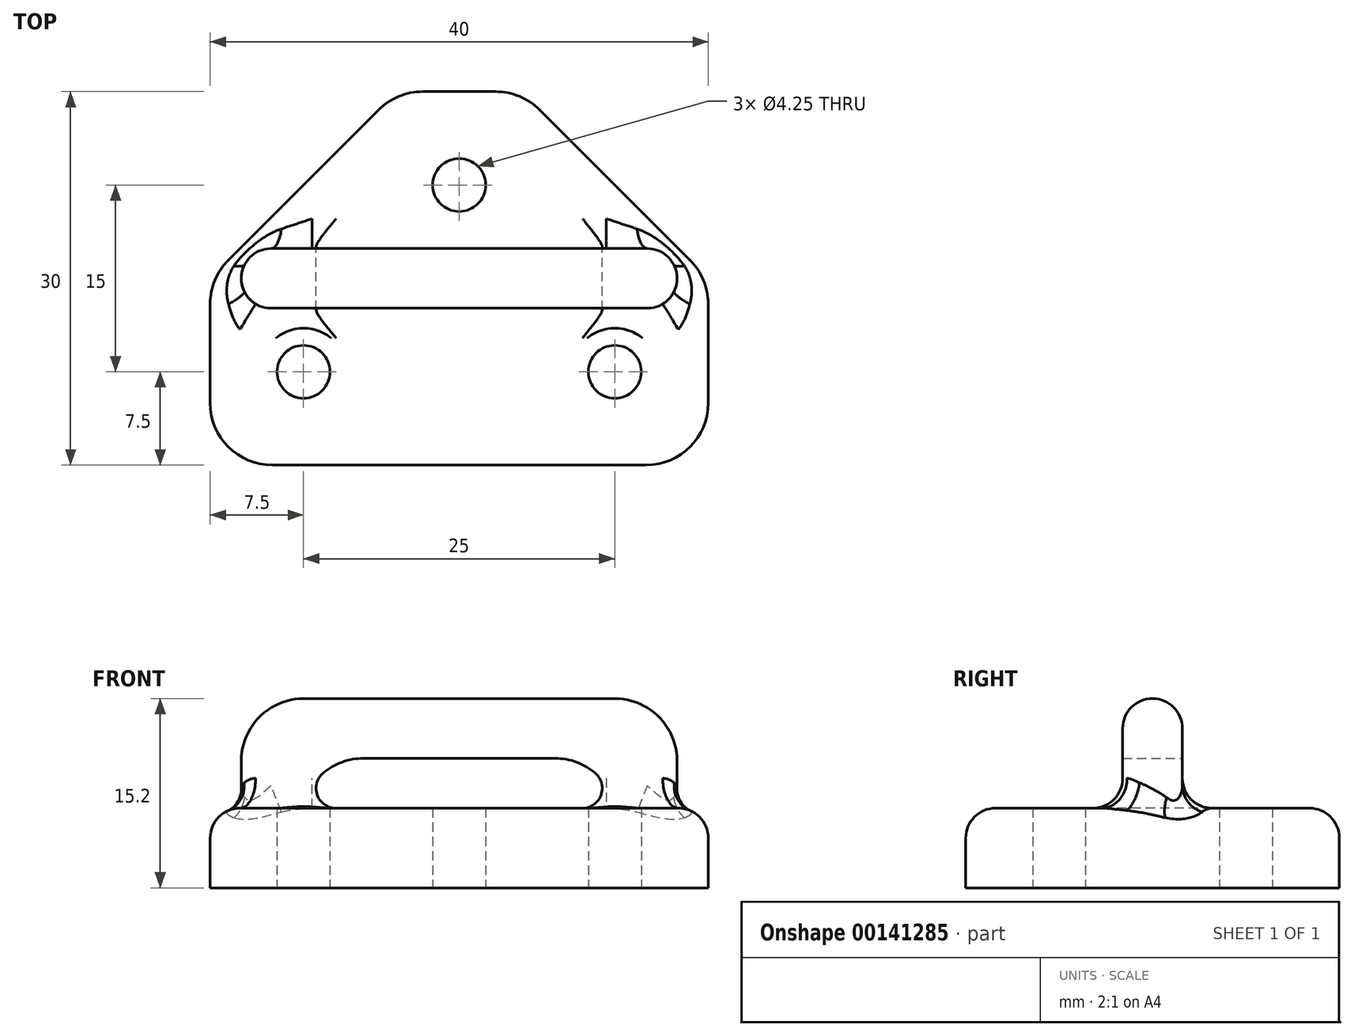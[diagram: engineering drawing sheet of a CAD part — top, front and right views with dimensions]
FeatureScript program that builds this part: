
annotation { "Feature Type Name" : "Feature", "Feature Type Description" : "" }
export const myFeature = defineFeature(function(context is Context, id is Id, definition is map)
    precondition{}
    {
        {
            var Q0;
            Q0=qCreatedBy(makeId("Top.planeOp"),FACE);
            var sketch = newSketch(context, id + "F0", { "sketchPlane" : qUnion([Q0])});
            skLineSegment(sketch, "E0.bottom", {"start": v(20, -15) * mm, "end": v(-20, -15) * mm});
            skLineSegment(sketch, "E0.top", {"start": v(20, 15) * mm, "end": v(-20, 15) * mm});
            skLineSegment(sketch, "E0.left", {"start": v(20, -15) * mm, "end": v(20, 15) * mm});
            skLineSegment(sketch, "E0.right", {"start": v(-20, -15) * mm, "end": v(-20, 15) * mm});
            skPoint(sketch, "E0.middle", {"position": v(0, 0) * mm});
            skCircle(sketch, "E1", {"center": v(0, 7.5) * mm, "radius": 2.12 * mm});
            skCircle(sketch, "E2", {"center": v(-12.5, -7.5) * mm, "radius": 2.12 * mm});
            skCircle(sketch, "E3.MirrorC", {"center": v(12.5, -7.5) * mm, "radius": 2.12 * mm});
            skSolve(sketch);
        }
        {
            var Q0;
            Q0 = qSketchRegion(id + "F0", true);
            extrude(context, id + "F1", {"entities" : qUnion([Q0]), "depth" : 6.4 * mm});
        }
        {
            var Q0;
            Q0=makeQuery(id+"F1.opExtrude","SWEPT_EDGE",EDGE,{"disambiguationData":[OSD([sQuery(id+"F0.wireOp",EDGE,"E0.top"),sQuery(id+"F0.wireOp",EDGE,"E0.right")])]});
            var Q1;
            Q1=makeQuery(id+"F1.opExtrude","SWEPT_EDGE",EDGE,{"disambiguationData":[OSD([sQuery(id+"F0.wireOp",EDGE,"E0.top"),sQuery(id+"F0.wireOp",EDGE,"E0.left")])]});
            chamfer(context, id + "F2", {"entities" : qUnion([Q0, Q1]), "width" : 15 * mm, "tangentPropagation" : true});
        }
        {
            var Q0;
            Q0=makeQuery(id+"F1.opExtrude","SWEPT_EDGE",EDGE,{"disambiguationData":[OSD([sQuery(id+"F0.wireOp",EDGE,"E0.bottom"),sQuery(id+"F0.wireOp",EDGE,"E0.right")])]});
            var Q1;
            Q1=makeQuery(id+"F1.opExtrude","SWEPT_EDGE",EDGE,{"disambiguationData":[OSD([sQuery(id+"F0.wireOp",EDGE,"E0.bottom"),sQuery(id+"F0.wireOp",EDGE,"E0.left")])]});
            var Q2;
            {var subQ0=sQuery(id+"F0.wireOp",EDGE,"E0.top");Q2=makeQuery(id+"F2.opChamfer","BLEND_EDGE",EDGE,{"blendedFrom":[makeQuery(id+"F1.opExtrude","SWEPT_EDGE",EDGE,{"disambiguationData":[OSD([subQ0,sQuery(id+"F0.wireOp",EDGE,"E0.right")])]}),makeQuery(id+"F1.opExtrude","SWEPT_FACE",FACE,{"disambiguationData":[OSD([subQ0])]})],"blendedInto":[makeQuery(id+"F1.opExtrude","SWEPT_FACE",FACE,{"disambiguationData":[OSD([subQ0])]})]});}
            var Q3;
            {var subQ0=sQuery(id+"F0.wireOp",EDGE,"E0.top");Q3=makeQuery(id+"F2.opChamfer","BLEND_EDGE",EDGE,{"blendedFrom":[makeQuery(id+"F1.opExtrude","SWEPT_EDGE",EDGE,{"disambiguationData":[OSD([subQ0,sQuery(id+"F0.wireOp",EDGE,"E0.left")])]}),makeQuery(id+"F1.opExtrude","SWEPT_FACE",FACE,{"disambiguationData":[OSD([subQ0])]})],"blendedInto":[makeQuery(id+"F1.opExtrude","SWEPT_FACE",FACE,{"disambiguationData":[OSD([subQ0])]})]});}
            var Q4;
            {var subQ0=sQuery(id+"F0.wireOp",EDGE,"E0.left");Q4=makeQuery(id+"F2.opChamfer","BLEND_EDGE",EDGE,{"blendedFrom":[makeQuery(id+"F1.opExtrude","SWEPT_EDGE",EDGE,{"disambiguationData":[OSD([sQuery(id+"F0.wireOp",EDGE,"E0.top"),subQ0])]}),makeQuery(id+"F1.opExtrude","SWEPT_FACE",FACE,{"disambiguationData":[OSD([subQ0])]})],"blendedInto":[makeQuery(id+"F1.opExtrude","SWEPT_FACE",FACE,{"disambiguationData":[OSD([subQ0])]})]});}
            var Q5;
            {var subQ0=sQuery(id+"F0.wireOp",EDGE,"E0.right");Q5=makeQuery(id+"F2.opChamfer","BLEND_EDGE",EDGE,{"blendedFrom":[makeQuery(id+"F1.opExtrude","SWEPT_EDGE",EDGE,{"disambiguationData":[OSD([sQuery(id+"F0.wireOp",EDGE,"E0.top"),subQ0])]}),makeQuery(id+"F1.opExtrude","SWEPT_FACE",FACE,{"disambiguationData":[OSD([subQ0])]})],"blendedInto":[makeQuery(id+"F1.opExtrude","SWEPT_FACE",FACE,{"disambiguationData":[OSD([subQ0])]})]});}
            fillet(context, id + "F3", {"entities" : qUnion([Q0, Q1, Q2, Q3, Q4, Q5]), "radius" : 5 * mm, "tangentPropagation" : true, "allowEdgeOverflow" : false});
        }
        {
            var Q0;
            Q0=qCreatedBy(makeId("Front.planeOp"),FACE);
            var sketch = newSketch(context, id + "F4", { "sketchPlane" : qUnion([Q0])});
            skLineSegment(sketch, "E4", {"start": v(-12.7, 6.4) * mm, "end": v(-17.5, 6.4) * mm});
            skLineSegment(sketch, "E5", {"start": v(-17.5, 6.4) * mm, "end": v(-17.5, 10.2) * mm});
            skLineSegment(sketch, "E6", {"start": v(-12.5, 15.2) * mm, "end": v(0, 15.2) * mm});
            skLineSegment(sketch, "E7", {"start": v(0, 10.4) * mm, "end": v(-7.7, 10.4) * mm});
            skLineSegment(sketch, "E8", {"start": v(-12.7, 6.4) * mm, "end": v(-12.7, 5.4) * mm});
            skPoint(sketch, "E9.orphan", {"position": v(0, 6.4) * mm});
            skLineSegment(sketch, "E10.MirrorCS", {"start": v(0, 10.4) * mm, "end": v(7.7, 10.4) * mm});
            skLineSegment(sketch, "E11.MirrorCS", {"start": v(17.5, 6.4) * mm, "end": v(17.5, 10.2) * mm});
            skLineSegment(sketch, "E12.MirrorCS", {"start": v(12.7, 6.4) * mm, "end": v(17.5, 6.4) * mm});
            skLineSegment(sketch, "E13.MirrorCS", {"start": v(12.5, 15.2) * mm, "end": v(0, 15.2) * mm});
            skLineSegment(sketch, "E14.MirrorCS", {"start": v(12.7, 6.4) * mm, "end": v(12.7, 5.4) * mm});
            skPoint(sketch, "E15.visualSharp", {"position": v(-17.5, 15.2) * mm});
            skArc(sketch, "E15.filletArc", {"start": v(-12.5, 15.2) * mm, "mid": v(-16.04, 13.74) * mm, "end": v(-17.5, 10.2) * mm});
            skPoint(sketch, "E16.visualSharp", {"position": v(17.5, 15.2) * mm});
            skArc(sketch, "E16.filletArc", {"start": v(17.5, 10.2) * mm, "mid": v(16.04, 13.74) * mm, "end": v(12.5, 15.2) * mm});
            skPoint(sketch, "E17.visualSharp", {"position": v(12.7, 10.4) * mm});
            skArc(sketch, "E17.filletArc", {"start": v(12.7, 5.4) * mm, "mid": v(11.24, 8.94) * mm, "end": v(7.7, 10.4) * mm});
            skPoint(sketch, "E18.visualSharp", {"position": v(-12.7, 10.4) * mm});
            skArc(sketch, "E18.filletArc", {"start": v(-7.7, 10.4) * mm, "mid": v(-11.24, 8.94) * mm, "end": v(-12.7, 5.4) * mm});
            skSolve(sketch);
        }
        {
            var Q0;
            Q0 = qSketchRegion(id + "F4", true);
            extrude(context, id + "F5", {"entities" : qUnion([Q0]), "operationType" : NewBodyOperationType.ADD, "endBound" : BoundingType.SYMMETRIC, "depth" : 4.8 * mm});
        }
        {
            var Q0;
            Q0=makeQuery(id+"F1.opExtrude","CAP_EDGE",EDGE,{"disambiguationData":[OSD([sQuery(id+"F0.wireOp",EDGE,"E0.top")])],"isStart":false});
            fillet(context, id + "F6", {"entities" : qUnion([Q0]), "radius" : 2.4 * mm, "tangentPropagation" : true, "allowEdgeOverflow" : false});
        }
        {
            var Q0;
            Q0=makeQuery(id+"F5.opExtrude","CAP_EDGE",EDGE,{"disambiguationData":[OSD([sQuery(id+"F4.wireOp",EDGE,"E6"),sQuery(id+"F4.wireOp",EDGE,"E13.MirrorCS")])],"isStart":true});
            var Q1;
            Q1=makeQuery(id+"F5.opExtrude","CAP_EDGE",EDGE,{"disambiguationData":[OSD([sQuery(id+"F4.wireOp",EDGE,"E6"),sQuery(id+"F4.wireOp",EDGE,"E13.MirrorCS")])],"isStart":false});
            fillet(context, id + "F7", {"entities" : qUnion([Q0, Q1]), "radius" : 2.4 * mm, "tangentPropagation" : true, "allowEdgeOverflow" : false});
        }
        {
            var Q0;
            Q0=makeQuery(id+"F5.boolean.opBoolean","INTERSECT",EDGE,{"derivedFrom":[makeQuery(id+"F1.opExtrude","CAP_FACE",FACE,{"disambiguationData":[OSD([sQuery(id+"F0.wireOp",EDGE,"E0.bottom"),sQuery(id+"F0.wireOp",EDGE,"E0.top"),sQuery(id+"F0.wireOp",EDGE,"E0.left"),sQuery(id+"F0.wireOp",EDGE,"E0.right"),sQuery(id+"F0.wireOp",EDGE,"E1"),sQuery(id+"F0.wireOp",EDGE,"E2"),sQuery(id+"F0.wireOp",EDGE,"E3.MirrorC")])],"isStart":false}),makeQuery(id+"F5.opExtrude","SWEPT_FACE",FACE,{"disambiguationData":[OSD([sQuery(id+"F4.wireOp",EDGE,"E17.filletArc")])]})]});
            var Q1;
            Q1=makeQuery(id+"F5.boolean.opBoolean","INTERSECT",EDGE,{"derivedFrom":[makeQuery(id+"F1.opExtrude","CAP_FACE",FACE,{"disambiguationData":[OSD([sQuery(id+"F0.wireOp",EDGE,"E0.bottom"),sQuery(id+"F0.wireOp",EDGE,"E0.top"),sQuery(id+"F0.wireOp",EDGE,"E0.left"),sQuery(id+"F0.wireOp",EDGE,"E0.right"),sQuery(id+"F0.wireOp",EDGE,"E1"),sQuery(id+"F0.wireOp",EDGE,"E2"),sQuery(id+"F0.wireOp",EDGE,"E3.MirrorC")])],"isStart":false}),makeQuery(id+"F5.opExtrude","SWEPT_FACE",FACE,{"disambiguationData":[OSD([sQuery(id+"F4.wireOp",EDGE,"E18.filletArc")])]})]});
            fillet(context, id + "F8", {"entities" : qUnion([Q0, Q1]), "radius" : 1.6 * mm, "tangentPropagation" : true, "allowEdgeOverflow" : false});
        }
        {
            var Q0;
            Q0=makeQuery(id+"F5.boolean.opBoolean","INTERSECT",EDGE,{"disambiguationData":[OD(0.0)],"derivedFrom":[makeQuery(id+"F1.opExtrude","CAP_FACE",FACE,{"disambiguationData":[OSD([sQuery(id+"F0.wireOp",EDGE,"E0.bottom"),sQuery(id+"F0.wireOp",EDGE,"E0.top"),sQuery(id+"F0.wireOp",EDGE,"E0.left"),sQuery(id+"F0.wireOp",EDGE,"E0.right"),sQuery(id+"F0.wireOp",EDGE,"E1"),sQuery(id+"F0.wireOp",EDGE,"E2"),sQuery(id+"F0.wireOp",EDGE,"E3.MirrorC")])],"isStart":false}),makeQuery(id+"F5.opExtrude","CAP_FACE",FACE,{"disambiguationData":[OSD([sQuery(id+"F4.wireOp",EDGE,"E4"),sQuery(id+"F4.wireOp",EDGE,"E5"),sQuery(id+"F4.wireOp",EDGE,"E6"),sQuery(id+"F4.wireOp",EDGE,"E7"),sQuery(id+"F4.wireOp",EDGE,"E8"),sQuery(id+"F4.wireOp",EDGE,"E10.MirrorCS"),sQuery(id+"F4.wireOp",EDGE,"E11.MirrorCS"),sQuery(id+"F4.wireOp",EDGE,"E12.MirrorCS"),sQuery(id+"F4.wireOp",EDGE,"E13.MirrorCS"),sQuery(id+"F4.wireOp",EDGE,"E14.MirrorCS"),sQuery(id+"F4.wireOp",EDGE,"E15.filletArc"),sQuery(id+"F4.wireOp",EDGE,"E16.filletArc"),sQuery(id+"F4.wireOp",EDGE,"E17.filletArc"),sQuery(id+"F4.wireOp",EDGE,"E18.filletArc")])],"isStart":false})]});
            var Q1;
            Q1=makeQuery(id+"F5.boolean.opBoolean","INTERSECT",EDGE,{"disambiguationData":[OD(1.0)],"derivedFrom":[makeQuery(id+"F1.opExtrude","CAP_FACE",FACE,{"disambiguationData":[OSD([sQuery(id+"F0.wireOp",EDGE,"E0.bottom"),sQuery(id+"F0.wireOp",EDGE,"E0.top"),sQuery(id+"F0.wireOp",EDGE,"E0.left"),sQuery(id+"F0.wireOp",EDGE,"E0.right"),sQuery(id+"F0.wireOp",EDGE,"E1"),sQuery(id+"F0.wireOp",EDGE,"E2"),sQuery(id+"F0.wireOp",EDGE,"E3.MirrorC")])],"isStart":false}),makeQuery(id+"F5.opExtrude","CAP_FACE",FACE,{"disambiguationData":[OSD([sQuery(id+"F4.wireOp",EDGE,"E4"),sQuery(id+"F4.wireOp",EDGE,"E5"),sQuery(id+"F4.wireOp",EDGE,"E6"),sQuery(id+"F4.wireOp",EDGE,"E7"),sQuery(id+"F4.wireOp",EDGE,"E8"),sQuery(id+"F4.wireOp",EDGE,"E10.MirrorCS"),sQuery(id+"F4.wireOp",EDGE,"E11.MirrorCS"),sQuery(id+"F4.wireOp",EDGE,"E12.MirrorCS"),sQuery(id+"F4.wireOp",EDGE,"E13.MirrorCS"),sQuery(id+"F4.wireOp",EDGE,"E14.MirrorCS"),sQuery(id+"F4.wireOp",EDGE,"E15.filletArc"),sQuery(id+"F4.wireOp",EDGE,"E16.filletArc"),sQuery(id+"F4.wireOp",EDGE,"E17.filletArc"),sQuery(id+"F4.wireOp",EDGE,"E18.filletArc")])],"isStart":false})]});
            fillet(context, id + "F9", {"entities" : qUnion([Q0, Q1]), "radius" : 2.4 * mm, "tangentPropagation" : true, "allowEdgeOverflow" : false});
        }
        {
            var Q0;
            Q0=makeQuery(id+"F1.opExtrude","CAP_FACE",FACE,{"disambiguationData":[OSD([sQuery(id+"F0.wireOp",EDGE,"E0.bottom"),sQuery(id+"F0.wireOp",EDGE,"E0.top"),sQuery(id+"F0.wireOp",EDGE,"E0.left"),sQuery(id+"F0.wireOp",EDGE,"E0.right"),sQuery(id+"F0.wireOp",EDGE,"E1"),sQuery(id+"F0.wireOp",EDGE,"E2"),sQuery(id+"F0.wireOp",EDGE,"E3.MirrorC")])],"isStart":false});
            var sketch = newSketch(context, id + "F10", { "sketchPlane" : qUnion([Q0])});
            skCircle(sketch, "E19", {"center": v(-12.5, -7.5) * mm, "radius": 3.5 * mm});
            skCircle(sketch, "E20.MirrorC", {"center": v(12.5, -7.5) * mm, "radius": 3.5 * mm});
            skSolve(sketch);
        }
        {
            var Q0;
            Q0 = qSketchRegion(id + "F10", true);
            extrude(context, id + "F11", {"entities" : qUnion([Q0]), "operationType" : NewBodyOperationType.REMOVE, "depth" : 25 * mm});
        }
    });
